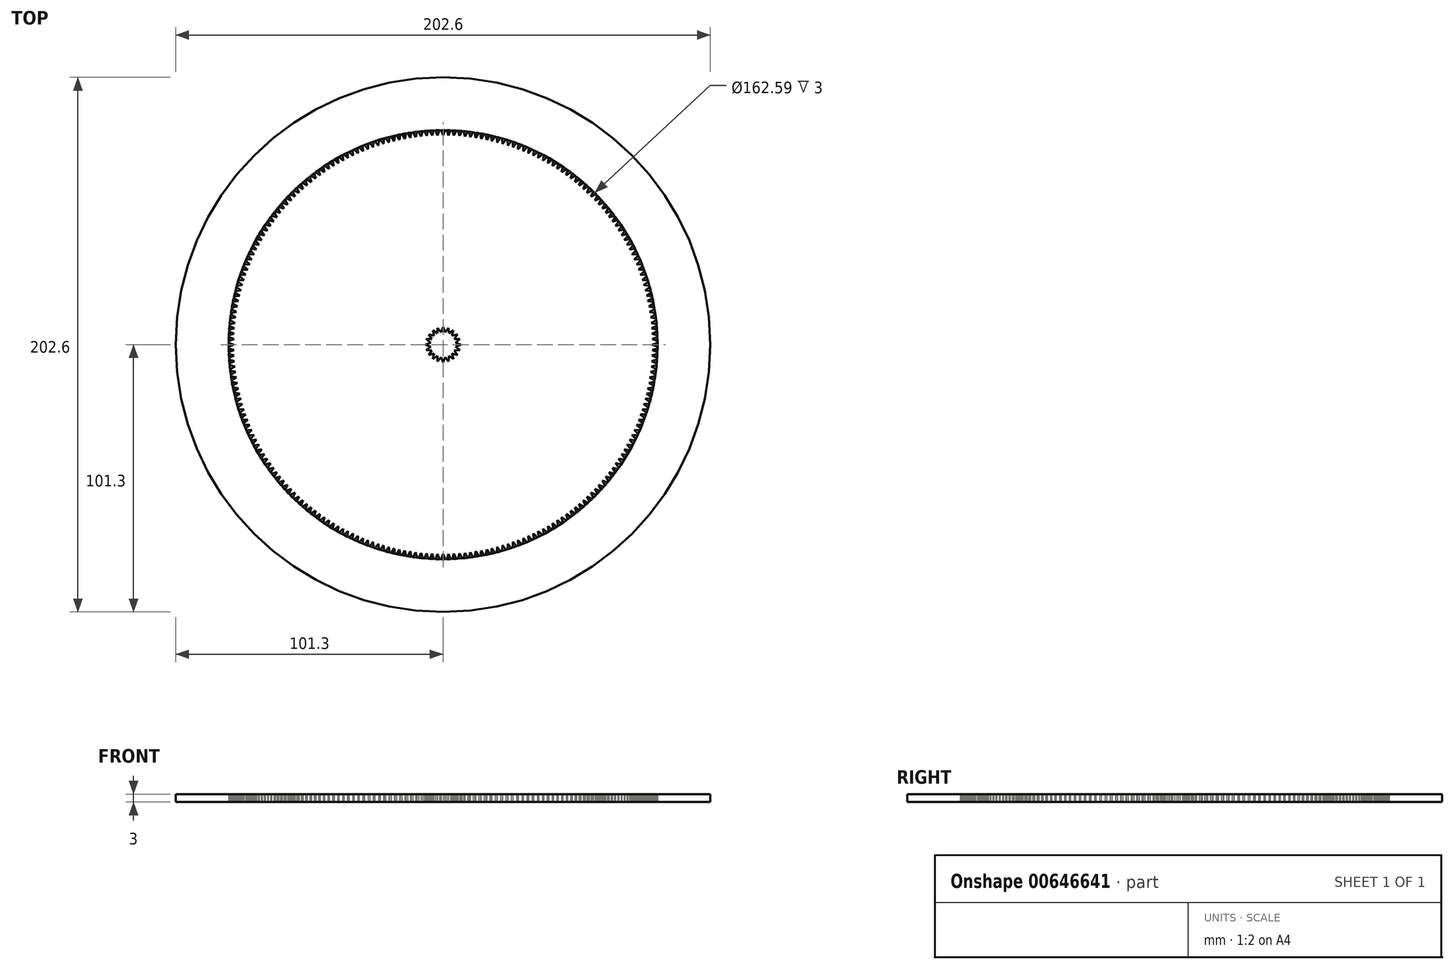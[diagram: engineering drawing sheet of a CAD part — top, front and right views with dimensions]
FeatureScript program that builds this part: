
annotation { "Feature Type Name" : "Feature", "Feature Type Description" : "" }
export const myFeature = defineFeature(function(context is Context, id is Id, definition is map)
    precondition{}
    {
        {
            assignVariable(context, id + "F0", {"variableType" : VariableType.NUMBER, "name" : "spur_teeth", "numberValue" : 20});
        }
        {
            var Q0;
            Q0=qCreatedBy(makeId("Top.planeOp"),FACE);
            var sketch = newSketch(context, id + "F1", { "sketchPlane" : qUnion([Q0])});
            skCircle(sketch, "E0", {"center": v(0, 0) * mm, "radius": 4.77 * mm});
            skLineSegment(sketch, "E1", {"start": v(-29.43, 0) * mm, "end": v(45.66, 0) * mm, "construction": true});
            skLineSegment(sketch, "E2", {"start": v(-4.72, 0.75) * mm, "end": v(-4.72, 0) * mm, "construction": true});
            skLineSegment(sketch, "E3", {"start": v(-4.72, 0) * mm, "end": v(-4.72, -0.75) * mm, "construction": true});
            skLineSegment(sketch, "E4", {"start": v(-4.72, 0.75) * mm, "end": v(-6.72, 0) * mm});
            skLineSegment(sketch, "E5", {"start": v(-6.72, 0) * mm, "end": v(-4.72, -0.75) * mm});
            skSolve(sketch);
        }
        {
            var Q0;
            {var subQ0=sQuery(id+"F1.wireOp",EDGE,"E0");var subQ1=makeQuery(id+"F1.imprint","INTERSECT",VERTEX,{"derivedFrom":[subQ0,sQuery(id+"F1.wireOp",EDGE,"E4")]});Q0=makeQuery(id+"F1.imprint","IMPRINT",FACE,{"disambiguationData":[TD([[makeQuery(id+"F1.imprint","IMPRINT",EDGE,{"disambiguationData":[TD([[subQ1,-1.0]])],"derivedFrom":subQ0}),1.0]])]});}
            extrude(context, id + "F2", {"entities" : qUnion([Q0]), "depth" : 3 * mm, "offsetDistance" : 25 * mm});
        }
        {
            var Q0;
            {var subQ0=sQuery(id+"F1.wireOp",EDGE,"E4");Q0=makeQuery(id+"F1.imprint","IMPRINT",FACE,{"disambiguationData":[TD([[makeQuery(id+"F1.imprint","IMPRINT",EDGE,{"derivedFrom":subQ0}),1.0]])]});}
            var Q1;
            Q1=makeQuery(id+"F2.opExtrude","CAP_FACE",FACE,{"disambiguationData":[OSD([sQuery(id+"F1.wireOp",EDGE,"E0")])],"isStart":false});
            extrude(context, id + "F3", {"entities" : qUnion([Q0]), "endBound" : BoundingType.UP_TO_SURFACE, "depth" : 25 * mm, "endBoundEntityFace" : qUnion([Q1]), "offsetDistance" : 25 * mm});
        }
        {
            var Q0;
            Q0=qCreatedBy(makeId("Right.planeOp"),FACE);
            var sketch = newSketch(context, id + "F4", { "sketchPlane" : qUnion([Q0])});
            skLineSegment(sketch, "E6", {"start": v(0, 0) * mm, "end": v(0, 59.89) * mm, "construction": true});
            skSolve(sketch);
        }
        {
            var Q0;
            Q0=makeQuery(id+"F3.opExtrude","SWEPT_BODY",BODY,{"disambiguationData":[OSD([sQuery(id+"F1.wireOp",EDGE,"E0"),sQuery(id+"F1.wireOp",EDGE,"E4"),sQuery(id+"F1.wireOp",EDGE,"E5")])]});
            var Q1;
            Q1=sQuery(id+"F4.wireOp",EDGE,"E6");
            circularPattern(context, id + "F5", {"operationType" : NewBodyOperationType.ADD, "entities" : qUnion([Q0]), "axis" : qUnion([Q1]), "angle" : 360 * degree, "instanceCount" : getVariable(context, 'spur_teeth'), "equalSpace" : true});
        }
        {
            var Q0;
            Q0=qCreatedBy(makeId("Top.planeOp"),FACE);
            var sketch = newSketch(context, id + "F6", { "sketchPlane" : qUnion([Q0])});
            skCircle(sketch, "E7", {"center": v(0, 0) * mm, "radius": 81.3 * mm});
            skCircle(sketch, "E8", {"center": v(0, 0) * mm, "radius": 101.3 * mm});
            skLineSegment(sketch, "E9", {"start": v(0, 0) * mm, "end": v(-219.63, 0) * mm, "construction": true});
            skLineSegment(sketch, "E10", {"start": v(-81.3, 0.75) * mm, "end": v(-81.3, 0) * mm});
            skLineSegment(sketch, "E11", {"start": v(-81.3, 0) * mm, "end": v(-81.3, -0.75) * mm});
            skLineSegment(sketch, "E12", {"start": v(-81.3, 0.75) * mm, "end": v(-79.3, 0) * mm});
            skLineSegment(sketch, "E13", {"start": v(-79.3, 0) * mm, "end": v(-81.3, -0.75) * mm});
            skSolve(sketch);
        }
        {
            var Q0;
            Q0=makeQuery(id+"F6.imprint","IMPRINT",FACE,{"disambiguationData":[TD([[makeQuery(id+"F6.imprint","IMPRINT",EDGE,{"derivedFrom":sQuery(id+"F6.wireOp",EDGE,"E8")}),1.0]])]});
            var Q1;
            {var subQ0=sQuery(id+"F1.wireOp",EDGE,"E0");var subQ1=makeQuery(id+"F3.opExtrude","CAP_FACE",FACE,{"disambiguationData":[OSD([subQ0,sQuery(id+"F1.wireOp",EDGE,"E4"),sQuery(id+"F1.wireOp",EDGE,"E5")])],"isStart":false});Q1=makeQuery(id+"F5.boolean.opBoolean","MERGE",FACE,{"derivedFrom":[makeQuery(id+"F2.opExtrude","CAP_FACE",FACE,{"disambiguationData":[OSD([subQ0])],"isStart":false}),subQ1,makeQuery(id+"F5.opPattern","COPY",FACE,{"derivedFrom":subQ1,"instanceName":"1"}),makeQuery(id+"F5.opPattern","COPY",FACE,{"derivedFrom":subQ1,"instanceName":"2"}),makeQuery(id+"F5.opPattern","COPY",FACE,{"derivedFrom":subQ1,"instanceName":"3"}),makeQuery(id+"F5.opPattern","COPY",FACE,{"derivedFrom":subQ1,"instanceName":"4"}),makeQuery(id+"F5.opPattern","COPY",FACE,{"derivedFrom":subQ1,"instanceName":"5"}),makeQuery(id+"F5.opPattern","COPY",FACE,{"derivedFrom":subQ1,"instanceName":"6"}),makeQuery(id+"F5.opPattern","COPY",FACE,{"derivedFrom":subQ1,"instanceName":"7"}),makeQuery(id+"F5.opPattern","COPY",FACE,{"derivedFrom":subQ1,"instanceName":"8"}),makeQuery(id+"F5.opPattern","COPY",FACE,{"derivedFrom":subQ1,"instanceName":"9"}),makeQuery(id+"F5.opPattern","COPY",FACE,{"derivedFrom":subQ1,"instanceName":"10"}),makeQuery(id+"F5.opPattern","COPY",FACE,{"derivedFrom":subQ1,"instanceName":"11"}),makeQuery(id+"F5.opPattern","COPY",FACE,{"derivedFrom":subQ1,"instanceName":"12"}),makeQuery(id+"F5.opPattern","COPY",FACE,{"derivedFrom":subQ1,"instanceName":"13"}),makeQuery(id+"F5.opPattern","COPY",FACE,{"derivedFrom":subQ1,"instanceName":"14"}),makeQuery(id+"F5.opPattern","COPY",FACE,{"derivedFrom":subQ1,"instanceName":"15"}),makeQuery(id+"F5.opPattern","COPY",FACE,{"derivedFrom":subQ1,"instanceName":"16"}),makeQuery(id+"F5.opPattern","COPY",FACE,{"derivedFrom":subQ1,"instanceName":"17"}),makeQuery(id+"F5.opPattern","COPY",FACE,{"derivedFrom":subQ1,"instanceName":"18"}),makeQuery(id+"F5.opPattern","COPY",FACE,{"derivedFrom":subQ1,"instanceName":"19"}),makeQuery(id+"F5.opPattern","COPY",FACE,{"derivedFrom":subQ1,"instanceName":"20"}),makeQuery(id+"F5.opPattern","COPY",FACE,{"derivedFrom":subQ1,"instanceName":"21"}),makeQuery(id+"F5.opPattern","COPY",FACE,{"derivedFrom":subQ1,"instanceName":"22"}),makeQuery(id+"F5.opPattern","COPY",FACE,{"derivedFrom":subQ1,"instanceName":"23"})]});}
            extrude(context, id + "F7", {"entities" : qUnion([Q0]), "endBound" : BoundingType.UP_TO_SURFACE, "depth" : 25 * mm, "endBoundEntityFace" : qUnion([Q1]), "offsetDistance" : 25 * mm});
        }
        {
            var Q0;
            Q0=makeQuery(id+"F6.imprint","IMPRINT",FACE,{"disambiguationData":[TD([[makeQuery(id+"F6.imprint","IMPRINT",EDGE,{"derivedFrom":sQuery(id+"F6.wireOp",EDGE,"E10")}),1.0]])]});
            var Q1;
            Q1=makeQuery(id+"F7.opExtrude","CAP_FACE",FACE,{"disambiguationData":[OSD([sQuery(id+"F6.wireOp",EDGE,"E7"),sQuery(id+"F6.wireOp",EDGE,"E8")])],"isStart":false});
            extrude(context, id + "F8", {"entities" : qUnion([Q0]), "endBound" : BoundingType.UP_TO_SURFACE, "depth" : 25 * mm, "endBoundEntityFace" : qUnion([Q1]), "offsetDistance" : 25 * mm});
        }
        {
            var Q0;
            Q0=makeQuery(id+"F8.opExtrude","SWEPT_BODY",BODY,{"disambiguationData":[OSD([sQuery(id+"F6.wireOp",EDGE,"E10"),sQuery(id+"F6.wireOp",EDGE,"E11"),sQuery(id+"F6.wireOp",EDGE,"E12"),sQuery(id+"F6.wireOp",EDGE,"E13")])]});
            var Q1;
            Q1=sQuery(id+"F4.wireOp",EDGE,"E6");
            circularPattern(context, id + "F9", {"operationType" : NewBodyOperationType.ADD, "entities" : qUnion([Q0]), "axis" : qUnion([Q1]), "angle" : 360 * degree, "instanceCount" : getVariable(context, 'spur_teeth') * 12, "equalSpace" : true});
        }
    });
